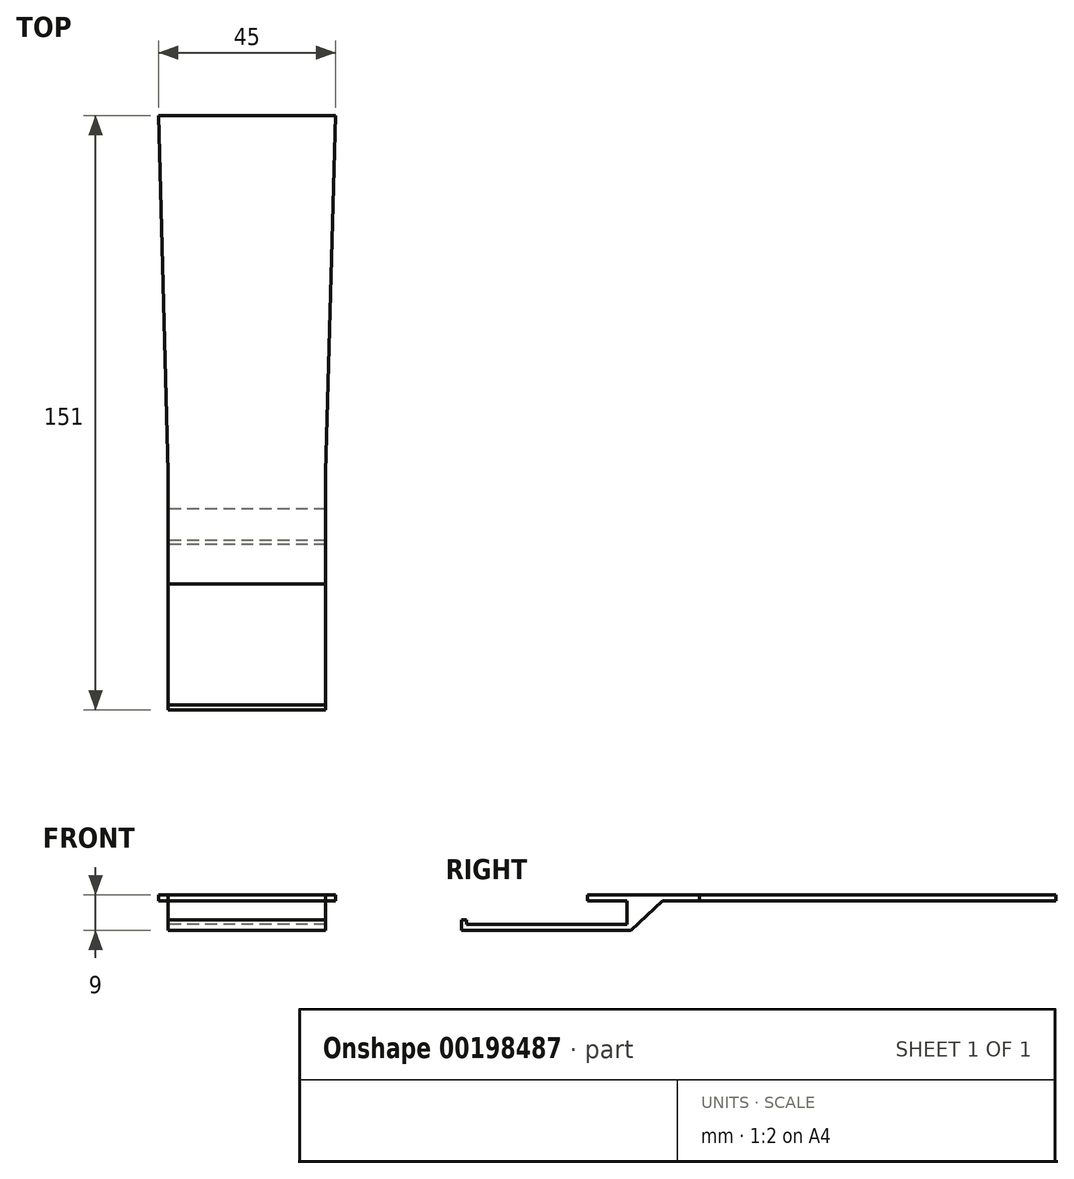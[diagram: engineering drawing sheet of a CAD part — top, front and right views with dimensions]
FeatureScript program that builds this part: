
annotation { "Feature Type Name" : "Feature", "Feature Type Description" : "" }
export const myFeature = defineFeature(function(context is Context, id is Id, definition is map)
    precondition{}
    {
        {
            var Q0;
            Q0=qCreatedBy(makeId("Right.planeOp"),FACE);
            var sketch = newSketch(context, id + "F0", { "sketchPlane" : qUnion([Q0])});
            skLineSegment(sketch, "E0", {"start": v(-53.17, 0) * mm, "end": v(65.83, 0) * mm});
            skLineSegment(sketch, "E1", {"start": v(-43.17, -7.5) * mm, "end": v(-43.17, -1.5) * mm});
            skLineSegment(sketch, "E2", {"start": v(-53.17, 0) * mm, "end": v(-53.17, -1.5) * mm});
            skLineSegment(sketch, "E3", {"start": v(-42.17, -9) * mm, "end": v(-85.17, -9) * mm});
            skLineSegment(sketch, "E4", {"start": v(-43.17, -1.5) * mm, "end": v(-53.17, -1.5) * mm});
            skLineSegment(sketch, "E5", {"start": v(-85.17, -9) * mm, "end": v(-85.17, -6.3) * mm});
            skLineSegment(sketch, "E6", {"start": v(-85.17, -6.3) * mm, "end": v(-83.97, -6.3) * mm});
            skLineSegment(sketch, "E7", {"start": v(-83.97, -6.3) * mm, "end": v(-83.97, -7.5) * mm});
            skLineSegment(sketch, "E8", {"start": v(-83.97, -7.5) * mm, "end": v(-43.17, -7.5) * mm});
            skLineSegment(sketch, "E9", {"start": v(-42.17, -9) * mm, "end": v(-34.17, -1.5) * mm});
            skLineSegment(sketch, "E10", {"start": v(65.83, -1.5) * mm, "end": v(65.83, 0) * mm});
            skLineSegment(sketch, "E11", {"start": v(65.83, -1.5) * mm, "end": v(-34.17, -1.5) * mm});
            skSolve(sketch);
        }
        {
            var Q0;
            Q0=makeQuery(id+"F0.imprint","IMPRINT",FACE,{"disambiguationData":[TD([[makeQuery(id+"F0.imprint","IMPRINT",EDGE,{"derivedFrom":sQuery(id+"F0.wireOp",EDGE,"E0")}),-1.0]])]});
            extrude(context, id + "F1", {"entities" : qUnion([Q0]), "endBound" : BoundingType.SYMMETRIC, "depth" : 45 * mm});
        }
        {
            var Q0;
            Q0=makeQuery(id+"F1.opExtrude","SWEPT_FACE",FACE,{"disambiguationData":[OSD([sQuery(id+"F0.wireOp",EDGE,"E0")])]});
            var sketch = newSketch(context, id + "F2", { "sketchPlane" : qUnion([Q0])});
            skLineSegment(sketch, "E12", {"start": v(0, -24.77) * mm, "end": v(22.5, -24.77) * mm, "construction": true});
            skLineSegment(sketch, "E13", {"start": v(0, 0) * mm, "end": v(0, -85.22) * mm, "construction": true});
            skLineSegment(sketch, "E14", {"start": v(-22.5, 65.83) * mm, "end": v(-20, -24.77) * mm});
            skPoint(sketch, "E14.endSnap0", {"position": v(11.25, -24.77) * mm});
            skLineSegment(sketch, "E15", {"start": v(-20, -24.77) * mm, "end": v(-20, -85.22) * mm});
            skLineSegment(sketch, "E16.MirrorCS", {"start": v(22.5, 65.83) * mm, "end": v(20, -24.77) * mm});
            skLineSegment(sketch, "E17.MirrorCS", {"start": v(20, -24.77) * mm, "end": v(20, -85.22) * mm});
            skLineSegment(sketch, "E18", {"start": v(-22.5, 65.83) * mm, "end": v(22.5, 65.83) * mm});
            skLineSegment(sketch, "E19", {"start": v(-20, -85.22) * mm, "end": v(20, -85.22) * mm});
            skSolve(sketch);
        }
        {
            var Q0;
            {var subQ5=sQuery(id+"F2.wireOp",EDGE,"E14");Q0=makeQuery(id+"F2.imprint","IMPRINT",FACE,{"disambiguationData":[TD([[makeQuery(id+"F2.imprint","IMPRINT",EDGE,{"derivedFrom":subQ5}),1.0]])]});}
            var Q1;
            {var subQ0=sQuery(id+"F2.wireOp",EDGE,"E19");Q1=makeQuery(id+"F2.imprint","IMPRINT",FACE,{"disambiguationData":[TD([[makeQuery(id+"F2.imprint","IMPRINT",EDGE,{"derivedFrom":subQ0}),1.0]])]});}
            extrude(context, id + "F3", {"entities" : qUnion([Q0, Q1]), "operationType" : NewBodyOperationType.INTERSECT, "oppositeDirection" : true, "depth" : 25 * mm});
        }
    });
